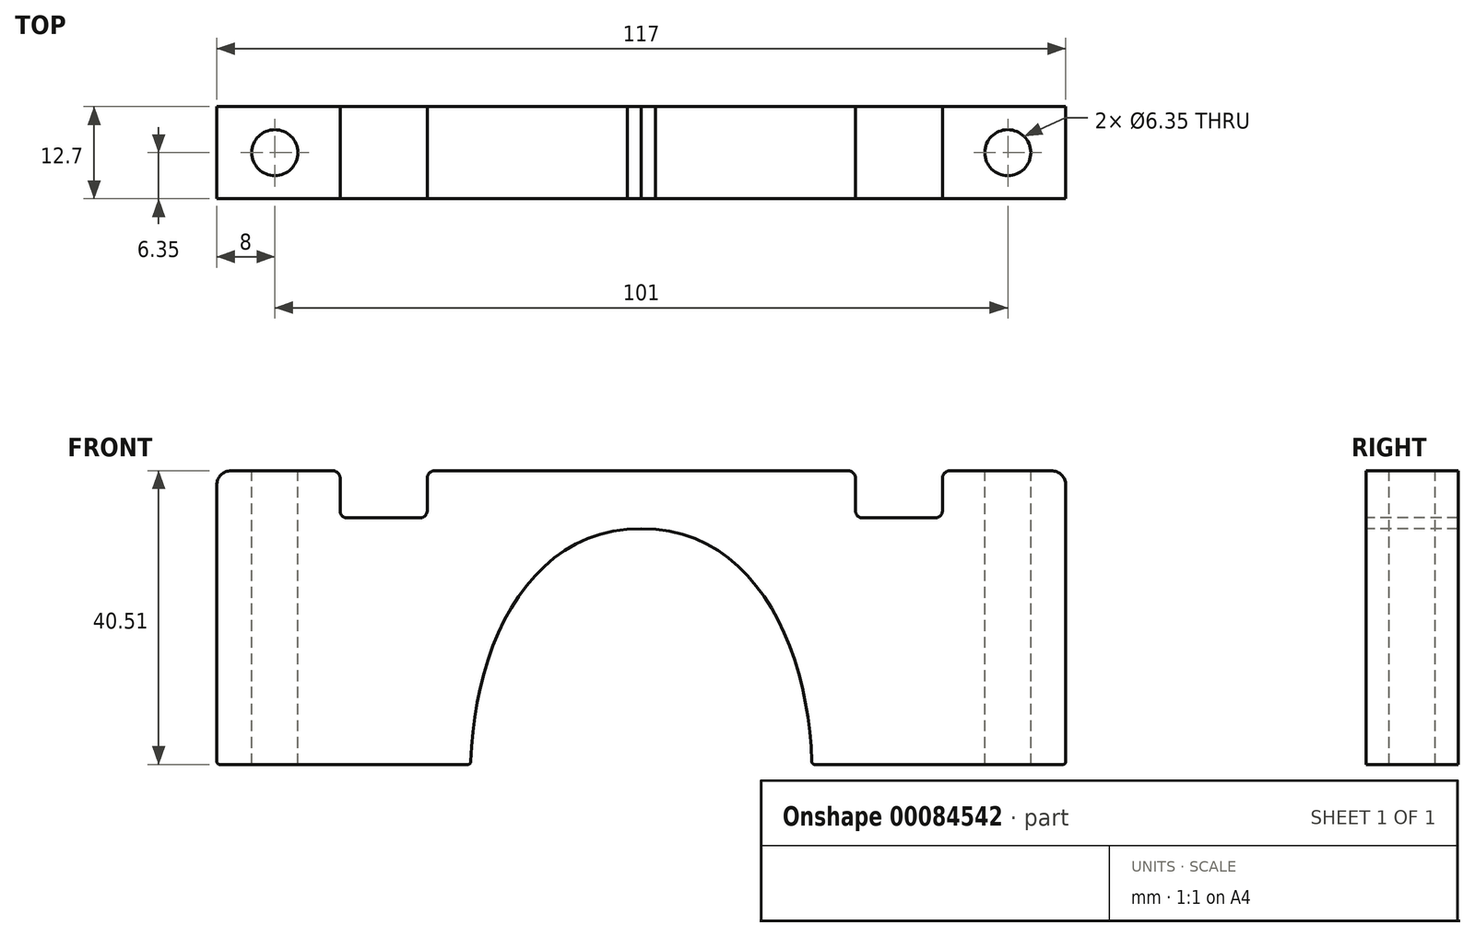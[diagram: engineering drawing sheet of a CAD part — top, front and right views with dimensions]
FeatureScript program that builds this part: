
annotation { "Feature Type Name" : "Feature", "Feature Type Description" : "" }
export const myFeature = defineFeature(function(context is Context, id is Id, definition is map)
    precondition{}
    {
        {
            var Q0;
            Q0=qCreatedBy(makeId("Front.planeOp"),FACE);
            var sketch = newSketch(context, id + "F0", { "sketchPlane" : qUnion([Q0]) });
            skPoint(sketch, "E0", {"position": v(0.8, 9.7) * mm});
            skPoint(sketch, "E1", {"position": v(2.4, 15.7) * mm});
            skPoint(sketch, "E2", {"position": v(6.6, 23.8) * mm});
            skPoint(sketch, "E3", {"position": v(12.9, 30.8) * mm});
            skPoint(sketch, "E4", {"position": v(19, 33.2) * mm});
            skPoint(sketch, "E5", {"position": v(23.5, 33.5) * mm});
            skLineSegment(sketch, "E6", {"start": v(23.5, 33.5) * mm, "end": v(23.5, 0) * mm, "construction": true});
            skPoint(sketch, "E7", {"position": v(3.4, 18.7) * mm});
            skPoint(sketch, "E8", {"position": v(9.6, 28) * mm});
            skFitSpline(sketch, "E9", {"points": [v(0, 0) * mm, v(23.5, 33.5) * mm], "startDerivative": vector(0, 48.1) * mm, "endDerivative": vector(48.2, -0.45) * mm});
            skFitSpline(sketch, "E10.MirrorCS", {"points": [v(47, 0) * mm, v(23.5, 33.5) * mm], "startDerivative": vector(0, 48.1) * mm, "endDerivative": vector(-48.2, -0.45) * mm});
            skFitSpline(sketch, "E11.0", {"points": [v(55, 0) * mm, v(55, 2.31) * mm, v(54.73, 6.98) * mm, v(53.5, 13.94) * mm, v(51.4, 20.7) * mm, v(48.31, 27.06) * mm, v(44.78, 31.86) * mm, v(41.28, 35.2) * mm, v(38.3, 37.4) * mm, v(34.99, 39.2) * mm, v(31.37, 40.54) * mm, v(27.5, 41.35) * mm, v(24.8, 41.51) * mm, v(23.42, 41.5) * mm]});
            skFitSpline(sketch, "E11.1", {"points": [v(-8, 0) * mm, v(-8, 2.31) * mm, v(-7.73, 6.98) * mm, v(-6.5, 13.94) * mm, v(-4.4, 20.7) * mm, v(-1.31, 27.06) * mm, v(2.22, 31.86) * mm, v(5.72, 35.2) * mm, v(8.7, 37.4) * mm, v(12.01, 39.2) * mm, v(15.63, 40.54) * mm, v(19.5, 41.35) * mm, v(22.2, 41.51) * mm, v(23.58, 41.5) * mm]});
            skLineSegment(sketch, "E12", {"start": v(0, 0) * mm, "end": v(-8, 0) * mm});
            skLineSegment(sketch, "E13.MirrorCS", {"start": v(47, 0) * mm, "end": v(55, 0) * mm});
            skLineSegment(sketch, "E14", {"start": v(-7.16, 10) * mm, "end": v(-35, 10) * mm});
            skLineSegment(sketch, "E15", {"start": v(-8, 0) * mm, "end": v(-35, 0) * mm});
            skLineSegment(sketch, "E16", {"start": v(-35, 0) * mm, "end": v(-35, 10) * mm});
            skLineSegment(sketch, "E17.MirrorCS", {"start": v(54.16, 10) * mm, "end": v(82, 10) * mm});
            skLineSegment(sketch, "E18.MirrorCS", {"start": v(82, 0) * mm, "end": v(82, 10) * mm});
            skLineSegment(sketch, "E19.MirrorCS", {"start": v(55, 0) * mm, "end": v(82, 0) * mm});
            skLineSegment(sketch, "E20", {"start": v(-35, 10) * mm, "end": v(-35, 41.5) * mm});
            skLineSegment(sketch, "E21", {"start": v(-35, 41.5) * mm, "end": v(23.5, 41.5) * mm});
            skLineSegment(sketch, "E22.MirrorCS", {"start": v(82, 10) * mm, "end": v(82, 41.5) * mm});
            skLineSegment(sketch, "E23.MirrorCS", {"start": v(82, 41.5) * mm, "end": v(23.5, 41.5) * mm});
            skPoint(sketch, "E24", {"position": v(-15, 41.5) * mm});
            skLineSegment(sketch, "E25", {"start": v(-15, 41.5) * mm, "end": v(-18, 41.5) * mm});
            skLineSegment(sketch, "E26", {"start": v(-18, 41.5) * mm, "end": v(-18, 38) * mm});
            skLineSegment(sketch, "E27", {"start": v(-18, 38) * mm, "end": v(-15, 38) * mm});
            skLineSegment(sketch, "E28", {"start": v(-15, 41.5) * mm, "end": v(-15, 38) * mm, "construction": true});
            skLineSegment(sketch, "E29.MirrorCS", {"start": v(-12, 38) * mm, "end": v(-15, 38) * mm});
            skLineSegment(sketch, "E30.MirrorCS", {"start": v(-12, 41.5) * mm, "end": v(-12, 38) * mm});
            skLineSegment(sketch, "E31.MirrorCS", {"start": v(-15, 41.5) * mm, "end": v(-12, 41.5) * mm});
            skSolve(sketch);
        }
        {
            var Q0;
            Q0=qSketchRegion(id+"F0",true);
            extrude(context, id + "F1", {"entities" : qUnion([Q0]), "depth" : 12.7 * mm});
        }
        {
            var Q0;
            Q0=makeQuery(id+"F1.opExtrude","SWEPT_FACE",FACE,{"disambiguationData":[OSD([sQuery(id+"F0.wireOp",EDGE,"E21")])]});
            var sketch = newSketch(context, id + "F2", { "sketchPlane" : qUnion([Q0]) });
            skCircle(sketch, "E32", {"center": v(-27, -6.35) * mm, "radius": 3.18 * mm});
            skPoint(sketch, "E32.centerSnap0", {"position": v(-35, -6.35) * mm});
            skCircle(sketch, "E33", {"center": v(74, -6.35) * mm, "radius": 3.18 * mm});
            skFitSpline(sketch, "E34.0", {"points": [v(23.5, -12.7) * mm, v(23.5, -8.47) * mm, v(23.5, -4.23) * mm, v(23.5, 0) * mm], "construction": true});
            skLineSegment(sketch, "E35.0", {"start": v(-35, 0) * mm, "end": v(23.1, 0) * mm});
            skLineSegment(sketch, "E35.1", {"start": v(-35, -12.7) * mm, "end": v(-35, 0) * mm});
            skLineSegment(sketch, "E35.2", {"start": v(-35, -12.7) * mm, "end": v(23.1, -12.7) * mm});
            skLineSegment(sketch, "E36", {"start": v(23.1, 0) * mm, "end": v(23.5, 0) * mm});
            skSolve(sketch);
        }
        {
            var Q0;
            Q0=qSketchRegion(id+"F2",true);
            var Q1;
            Q1=makeQuery(id+"F1.opExtrude","SWEPT_FACE",FACE,{"disambiguationData":[OSD([sQuery(id+"F0.wireOp",EDGE,"E13.MirrorCS"),sQuery(id+"F0.wireOp",EDGE,"E19.MirrorCS")])]});
            extrude(context, id + "F3", {"entities" : qUnion([Q0]), "operationType" : NewBodyOperationType.REMOVE, "endBound" : BoundingType.UP_TO_SURFACE, "oppositeDirection" : true, "endBoundEntityFace" : qUnion([Q1]), "depth" : 100 * mm});
        }
        {
            var Q0;
            Q0=qCreatedBy(makeId("Front.planeOp"),FACE);
            var sketch = newSketch(context, id + "F4", { "sketchPlane" : qUnion([Q0]) });
            skLineSegment(sketch, "E37.bottom", {"start": v(-42.44, 1) * mm, "end": v(87.98, 1) * mm});
            skLineSegment(sketch, "E37.top", {"start": v(-42.44, -3.1) * mm, "end": v(87.98, -3.1) * mm});
            skLineSegment(sketch, "E37.left", {"start": v(-42.44, 1) * mm, "end": v(-42.44, -3.1) * mm});
            skLineSegment(sketch, "E37.right", {"start": v(87.98, 1) * mm, "end": v(87.98, -3.1) * mm});
            skSolve(sketch);
        }
        {
            var Q0;
            Q0=qSketchRegion(id+"F4",true);
            extrude(context, id + "F5", {"entities" : qUnion([Q0]), "operationType" : NewBodyOperationType.REMOVE, "depth" : 25 * mm});
        }
        {
            var Q0;
            Q0=makeQuery(id+"F1.opExtrude","SWEPT_EDGE",EDGE,{"disambiguationData":[OSD([sQuery(id+"F0.wireOp",EDGE,"E22.MirrorCS"),sQuery(id+"F0.wireOp",EDGE,"E23.MirrorCS")])]});
            var Q1;
            Q1=makeQuery(id+"F1.opExtrude","SWEPT_EDGE",EDGE,{"disambiguationData":[OSD([sQuery(id+"F0.wireOp",EDGE,"E20"),sQuery(id+"F0.wireOp",EDGE,"E21")])]});
            fillet(context, id + "F6", {"entities" : qUnion([Q0, Q1]), "radius" : 2 * mm, "tangentPropagation" : true, "conicFillet" : false});
        }
        {
            var Q0;
            Q0=makeQuery(id+"F5.boolean.opBoolean","INTERSECT",EDGE,{"derivedFrom":[makeQuery(id+"F1.opExtrude","SWEPT_FACE",FACE,{"disambiguationData":[OSD([sQuery(id+"F0.wireOp",EDGE,"E16"),sQuery(id+"F0.wireOp",EDGE,"E20")])]}),makeQuery(id+"F5.opExtrude","SWEPT_FACE",FACE,{"disambiguationData":[OSD([sQuery(id+"F4.wireOp",EDGE,"E37.bottom")])]})]});
            var Q1;
            Q1=makeQuery(id+"F5.boolean.opBoolean","INTERSECT",EDGE,{"derivedFrom":[makeQuery(id+"F1.opExtrude","SWEPT_FACE",FACE,{"disambiguationData":[OSD([sQuery(id+"F0.wireOp",EDGE,"E9")])]}),makeQuery(id+"F5.opExtrude","SWEPT_FACE",FACE,{"disambiguationData":[OSD([sQuery(id+"F4.wireOp",EDGE,"E37.bottom")])]})]});
            var Q2;
            Q2=makeQuery(id+"F5.boolean.opBoolean","INTERSECT",EDGE,{"derivedFrom":[makeQuery(id+"F1.opExtrude","SWEPT_FACE",FACE,{"disambiguationData":[OSD([sQuery(id+"F0.wireOp",EDGE,"E10.MirrorCS")])]}),makeQuery(id+"F5.opExtrude","SWEPT_FACE",FACE,{"disambiguationData":[OSD([sQuery(id+"F4.wireOp",EDGE,"E37.bottom")])]})]});
            var Q3;
            Q3=makeQuery(id+"F5.boolean.opBoolean","INTERSECT",EDGE,{"derivedFrom":[makeQuery(id+"F1.opExtrude","SWEPT_FACE",FACE,{"disambiguationData":[OSD([sQuery(id+"F0.wireOp",EDGE,"E18.MirrorCS"),sQuery(id+"F0.wireOp",EDGE,"E22.MirrorCS")])]}),makeQuery(id+"F5.opExtrude","SWEPT_FACE",FACE,{"disambiguationData":[OSD([sQuery(id+"F4.wireOp",EDGE,"E37.bottom")])]})]});
            fillet(context, id + "F7", {"entities" : qUnion([Q0, Q1, Q2, Q3]), "radius" : .432 * mm, "tangentPropagation" : true, "conicFillet" : false});
        }
        {
            var Q0;
            Q0=makeQuery(id+"F1.opExtrude","CAP_FACE",FACE,{"disambiguationData":[OSD([sQuery(id+"F0.wireOp",EDGE,"E9"),sQuery(id+"F0.wireOp",EDGE,"E10.MirrorCS"),sQuery(id+"F0.wireOp",EDGE,"E11.0"),sQuery(id+"F0.wireOp",EDGE,"E11.1"),sQuery(id+"F0.wireOp",EDGE,"E12"),sQuery(id+"F0.wireOp",EDGE,"E13.MirrorCS"),sQuery(id+"F0.wireOp",EDGE,"E15"),sQuery(id+"F0.wireOp",EDGE,"E16"),sQuery(id+"F0.wireOp",EDGE,"E18.MirrorCS"),sQuery(id+"F0.wireOp",EDGE,"E19.MirrorCS"),sQuery(id+"F0.wireOp",EDGE,"E20"),sQuery(id+"F0.wireOp",EDGE,"E21"),sQuery(id+"F0.wireOp",EDGE,"E22.MirrorCS"),sQuery(id+"F0.wireOp",EDGE,"E23.MirrorCS"),sQuery(id+"F0.wireOp",EDGE,"E25"),sQuery(id+"F0.wireOp",EDGE,"E31.MirrorCS")])],"isStart":false});
            var sketch = newSketch(context, id + "F8", { "sketchPlane" : qUnion([Q0]) });
            skPoint(sketch, "E38", {"position": v(-12, 41.5) * mm});
            skLineSegment(sketch, "E39", {"start": v(-12, 41.5) * mm, "end": v(-12, 35) * mm, "construction": true});
            skLineSegment(sketch, "E40", {"start": v(-12, 35) * mm, "end": v(-18, 35) * mm});
            skLineSegment(sketch, "E41", {"start": v(-18, 35) * mm, "end": v(-18, 41.5) * mm});
            skLineSegment(sketch, "E42", {"start": v(-18, 41.5) * mm, "end": v(-12, 41.5) * mm});
            skLineSegment(sketch, "E43.MirrorCS", {"start": v(-6, 41.5) * mm, "end": v(-12, 41.5) * mm});
            skLineSegment(sketch, "E44.MirrorCS", {"start": v(-6, 35) * mm, "end": v(-6, 41.5) * mm});
            skLineSegment(sketch, "E45.MirrorCS", {"start": v(-12, 35) * mm, "end": v(-6, 35) * mm});
            skPoint(sketch, "E46", {"position": v(23.5, 41.5) * mm});
            skLineSegment(sketch, "E47", {"start": v(23.5, 41.5) * mm, "end": v(23.5, 0) * mm, "construction": true});
            skLineSegment(sketch, "E48.MirrorCS", {"start": v(59, 41.5) * mm, "end": v(59, 35) * mm, "construction": true});
            skPoint(sketch, "E49.MirrorP", {"position": v(59, 41.5) * mm});
            skLineSegment(sketch, "E50.MirrorCS", {"start": v(65, 35) * mm, "end": v(65, 41.5) * mm});
            skLineSegment(sketch, "E51.MirrorCS", {"start": v(65, 41.5) * mm, "end": v(59, 41.5) * mm});
            skLineSegment(sketch, "E52.MirrorCS", {"start": v(53, 41.5) * mm, "end": v(59, 41.5) * mm});
            skLineSegment(sketch, "E53.MirrorCS", {"start": v(59, 35) * mm, "end": v(53, 35) * mm});
            skLineSegment(sketch, "E54.MirrorCS", {"start": v(53, 35) * mm, "end": v(53, 41.5) * mm});
            skLineSegment(sketch, "E55.MirrorCS", {"start": v(59, 35) * mm, "end": v(65, 35) * mm});
            skSolve(sketch);
        }
        {
            var Q0;
            Q0=qSketchRegion(id+"F8",true);
            var Q1;
            Q1=makeQuery(id+"F1.opExtrude","CAP_FACE",FACE,{"disambiguationData":[OSD([sQuery(id+"F0.wireOp",EDGE,"E9"),sQuery(id+"F0.wireOp",EDGE,"E10.MirrorCS"),sQuery(id+"F0.wireOp",EDGE,"E11.0"),sQuery(id+"F0.wireOp",EDGE,"E11.1"),sQuery(id+"F0.wireOp",EDGE,"E12"),sQuery(id+"F0.wireOp",EDGE,"E13.MirrorCS"),sQuery(id+"F0.wireOp",EDGE,"E15"),sQuery(id+"F0.wireOp",EDGE,"E16"),sQuery(id+"F0.wireOp",EDGE,"E18.MirrorCS"),sQuery(id+"F0.wireOp",EDGE,"E19.MirrorCS"),sQuery(id+"F0.wireOp",EDGE,"E20"),sQuery(id+"F0.wireOp",EDGE,"E21"),sQuery(id+"F0.wireOp",EDGE,"E22.MirrorCS"),sQuery(id+"F0.wireOp",EDGE,"E23.MirrorCS"),sQuery(id+"F0.wireOp",EDGE,"E25"),sQuery(id+"F0.wireOp",EDGE,"E31.MirrorCS")])],"isStart":true});
            extrude(context, id + "F9", {"entities" : qUnion([Q0]), "operationType" : NewBodyOperationType.REMOVE, "endBound" : BoundingType.UP_TO_SURFACE, "oppositeDirection" : true, "endBoundEntityFace" : qUnion([Q1]), "depth" : 25 * mm});
        }
        {
            var Q0;
            Q0=makeQuery(id+"F9.boolean.opBoolean","COPY",EDGE,{"derivedFrom":makeQuery(id+"F9.opExtrude","SWEPT_EDGE",EDGE,{"disambiguationData":[OSD([sQuery(id+"F8.wireOp",EDGE,"E40"),sQuery(id+"F8.wireOp",EDGE,"E41")])]})});
            var Q1;
            Q1=makeQuery(id+"F9.boolean.opBoolean","COPY",EDGE,{"derivedFrom":makeQuery(id+"F9.opExtrude","SWEPT_EDGE",EDGE,{"disambiguationData":[OSD([sQuery(id+"F8.wireOp",EDGE,"E44.MirrorCS"),sQuery(id+"F8.wireOp",EDGE,"E45.MirrorCS")])]})});
            var Q2;
            Q2=makeQuery(id+"F9.boolean.opBoolean","COPY",EDGE,{"derivedFrom":makeQuery(id+"F9.opExtrude","SWEPT_EDGE",EDGE,{"disambiguationData":[OSD([sQuery(id+"F0.wireOp",EDGE,"E21"),sQuery(id+"F0.wireOp",EDGE,"E25"),sQuery(id+"F0.wireOp",EDGE,"E31.MirrorCS"),sQuery(id+"F8.wireOp",EDGE,"E41"),sQuery(id+"F8.wireOp",EDGE,"E42")])]})});
            var Q3;
            Q3=makeQuery(id+"F9.boolean.opBoolean","COPY",EDGE,{"derivedFrom":makeQuery(id+"F9.opExtrude","SWEPT_EDGE",EDGE,{"disambiguationData":[OSD([sQuery(id+"F0.wireOp",EDGE,"E21"),sQuery(id+"F0.wireOp",EDGE,"E25"),sQuery(id+"F0.wireOp",EDGE,"E31.MirrorCS"),sQuery(id+"F8.wireOp",EDGE,"E43.MirrorCS"),sQuery(id+"F8.wireOp",EDGE,"E44.MirrorCS")])]})});
            var Q4;
            Q4=makeQuery(id+"F9.boolean.opBoolean","COPY",EDGE,{"derivedFrom":makeQuery(id+"F9.opExtrude","SWEPT_EDGE",EDGE,{"disambiguationData":[OSD([sQuery(id+"F8.wireOp",EDGE,"E53.MirrorCS"),sQuery(id+"F8.wireOp",EDGE,"E54.MirrorCS")])]})});
            var Q5;
            Q5=makeQuery(id+"F9.boolean.opBoolean","COPY",EDGE,{"derivedFrom":makeQuery(id+"F9.opExtrude","SWEPT_EDGE",EDGE,{"disambiguationData":[OSD([sQuery(id+"F0.wireOp",EDGE,"E23.MirrorCS"),sQuery(id+"F8.wireOp",EDGE,"E52.MirrorCS"),sQuery(id+"F8.wireOp",EDGE,"E54.MirrorCS")])]})});
            var Q6;
            Q6=makeQuery(id+"F9.boolean.opBoolean","COPY",EDGE,{"derivedFrom":makeQuery(id+"F9.opExtrude","SWEPT_EDGE",EDGE,{"disambiguationData":[OSD([sQuery(id+"F8.wireOp",EDGE,"E50.MirrorCS"),sQuery(id+"F8.wireOp",EDGE,"E55.MirrorCS")])]})});
            var Q7;
            Q7=makeQuery(id+"F9.boolean.opBoolean","COPY",EDGE,{"derivedFrom":makeQuery(id+"F9.opExtrude","SWEPT_EDGE",EDGE,{"disambiguationData":[OSD([sQuery(id+"F0.wireOp",EDGE,"E23.MirrorCS"),sQuery(id+"F8.wireOp",EDGE,"E50.MirrorCS"),sQuery(id+"F8.wireOp",EDGE,"E51.MirrorCS")])]})});
            fillet(context, id + "F10", {"entities" : qUnion([Q0, Q1, Q2, Q3, Q4, Q5, Q6, Q7]), "radius" : 1 * mm, "tangentPropagation" : true, "conicFillet" : false});
        }
    });
